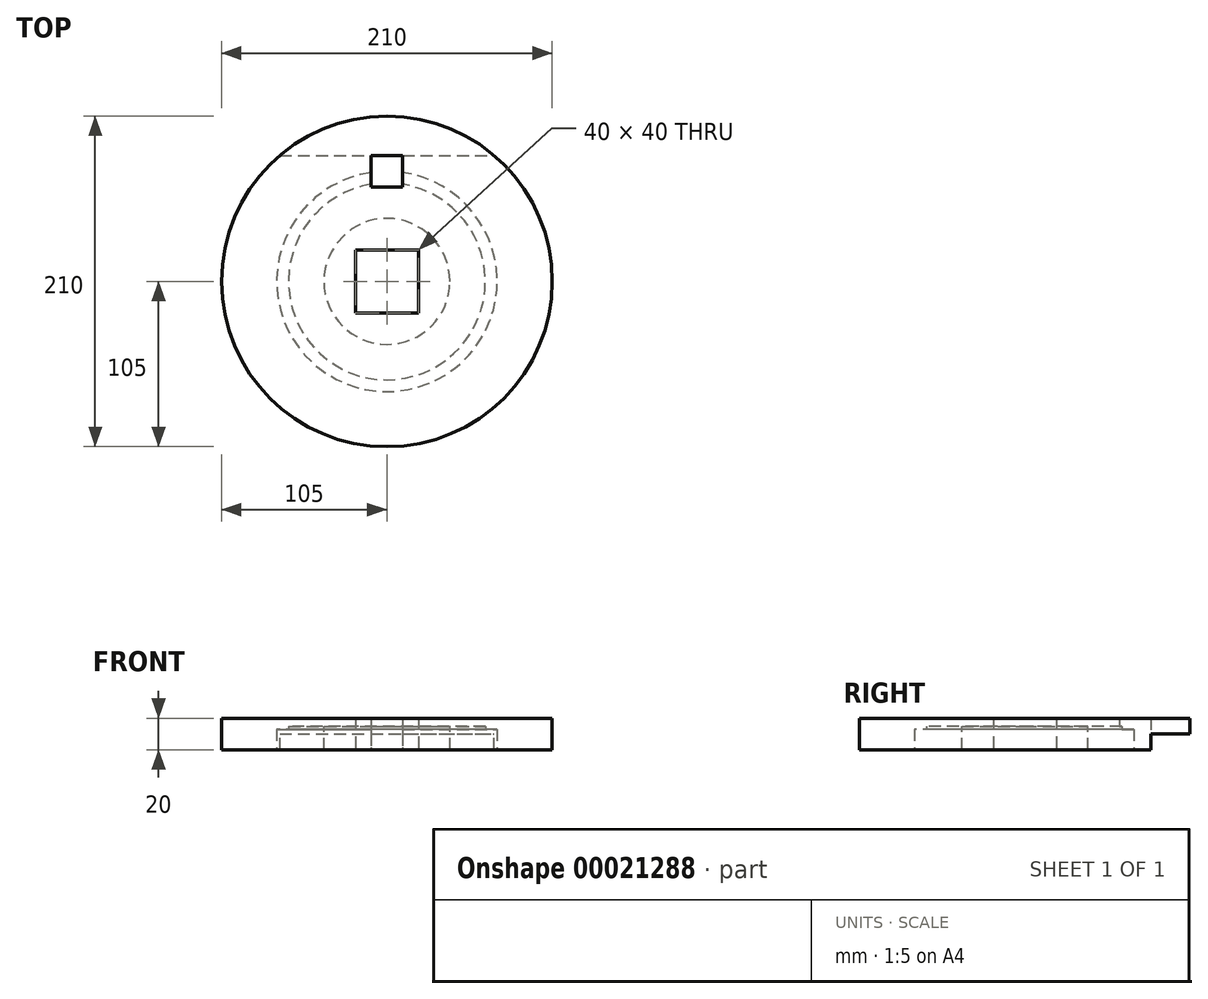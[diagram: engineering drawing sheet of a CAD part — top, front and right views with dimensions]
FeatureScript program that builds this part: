
annotation { "Feature Type Name" : "Feature", "Feature Type Description" : "" }
export const myFeature = defineFeature(function(context is Context, id is Id, definition is map)
    precondition{}
    {
        {
            var Q0;
            Q0=qCreatedBy(makeId("Top.planeOp"),FACE);
            var sketch = newSketch(context, id + "F0", { "sketchPlane" : qUnion([Q0])});
            skCircle(sketch, "E0", {"center": v(0, 0) * mm, "radius": 105 * mm});
            skSolve(sketch);
        }
        {
            var Q0;
            Q0=makeQuery(id+"F0.imprint","IMPRINT",FACE,{"disambiguationData":[TD([[makeQuery(id+"F0.imprint","IMPRINT",EDGE,{"derivedFrom":sQuery(id+"F0.wireOp",EDGE,"E0")}),1.0]])]});
            extrude(context, id + "F1", {"entities" : qUnion([Q0]), "oppositeDirection" : true, "depth" : 20 * mm});
        }
        {
            var Q0;
            Q0=makeQuery(id+"F1.opExtrude","CAP_FACE",FACE,{"disambiguationData":[OSD([sQuery(id+"F0.wireOp",EDGE,"E0")])],"isStart":false});
            var sketch = newSketch(context, id + "F2", { "sketchPlane" : qUnion([Q0])});
            skCircle(sketch, "E1", {"center": v(0, 0) * mm, "radius": 70 * mm});
            skSolve(sketch);
        }
        {
            var Q0;
            Q0 = qSketchRegion(id + "F2", true);
            extrude(context, id + "F3", {"entities" : qUnion([Q0]), "operationType" : NewBodyOperationType.REMOVE, "oppositeDirection" : true, "depth" : 13 * mm});
        }
        {
            var Q0;
            Q0=makeQuery(id+"F3.boolean.opBoolean","COPY",FACE,{"derivedFrom":makeQuery(id+"F3.opExtrude","CAP_FACE",FACE,{"disambiguationData":[OSD([sQuery(id+"F2.wireOp",EDGE,"E1")])],"isStart":false})});
            var sketch = newSketch(context, id + "F4", { "sketchPlane" : qUnion([Q0])});
            skCircle(sketch, "E2", {"center": v(0, 0) * mm, "radius": 62.5 * mm});
            skSolve(sketch);
        }
        {
            var Q0;
            Q0 = qSketchRegion(id + "F4", true);
            extrude(context, id + "F5", {"entities" : qUnion([Q0]), "operationType" : NewBodyOperationType.REMOVE, "oppositeDirection" : true, "depth" : 2 * mm});
        }
        {
            var Q0;
            Q0=makeQuery(id+"F5.boolean.opBoolean","COPY",FACE,{"derivedFrom":makeQuery(id+"F5.opExtrude","CAP_FACE",FACE,{"disambiguationData":[OSD([sQuery(id+"F4.wireOp",EDGE,"E2")])],"isStart":false})});
            var sketch = newSketch(context, id + "F6", { "sketchPlane" : qUnion([Q0])});
            skCircle(sketch, "E3", {"center": v(0, 0) * mm, "radius": 40 * mm});
            skSolve(sketch);
        }
        {
            var Q0;
            Q0 = qSketchRegion(id + "F6", true);
            extrude(context, id + "F7", {"entities" : qUnion([Q0]), "operationType" : NewBodyOperationType.ADD, "depth" : 15 * mm});
        }
        {
            var Q0;
            Q0=makeQuery(id+"F7.opExtrude","CAP_FACE",FACE,{"disambiguationData":[OSD([sQuery(id+"F6.wireOp",EDGE,"E3")])],"isStart":false});
            var sketch = newSketch(context, id + "F8", { "sketchPlane" : qUnion([Q0])});
            skLineSegment(sketch, "E4.rect.bottom", {"start": v(20, -20) * mm, "end": v(-20, -20) * mm});
            skLineSegment(sketch, "E4.rect.top", {"start": v(20, 20) * mm, "end": v(-20, 20) * mm});
            skLineSegment(sketch, "E4.rect.left", {"start": v(20, -20) * mm, "end": v(20, 20) * mm});
            skLineSegment(sketch, "E4.rect.right", {"start": v(-20, -20) * mm, "end": v(-20, 20) * mm});
            skPoint(sketch, "E4.rect.middle", {"position": v(0, 0) * mm});
            skSolve(sketch);
        }
        {
            var Q0;
            Q0 = qSketchRegion(id + "F8", true);
            var Q1;
            Q1=makeQuery(id+"F1.opExtrude","CAP_FACE",FACE,{"disambiguationData":[OSD([sQuery(id+"F0.wireOp",EDGE,"E0")])],"isStart":true});
            extrude(context, id + "F9", {"entities" : qUnion([Q0]), "operationType" : NewBodyOperationType.REMOVE, "endBound" : BoundingType.UP_TO_SURFACE, "oppositeDirection" : true, "endBoundEntityFace" : qUnion([Q1]), "depth" : 25 * mm});
        }
        {
            var Q0;
            Q0=makeQuery(id+"F1.opExtrude","CAP_FACE",FACE,{"disambiguationData":[OSD([sQuery(id+"F0.wireOp",EDGE,"E0")])],"isStart":false});
            var sketch = newSketch(context, id + "F10", { "sketchPlane" : qUnion([Q0])});
            skLineSegment(sketch, "E5.bottom", {"start": v(-10, -60) * mm, "end": v(10, -60) * mm});
            skLineSegment(sketch, "E5.top", {"start": v(-10, -80) * mm, "end": v(10, -80) * mm});
            skLineSegment(sketch, "E5.left", {"start": v(-10, -60) * mm, "end": v(-10, -80) * mm});
            skLineSegment(sketch, "E5.right", {"start": v(10, -60) * mm, "end": v(10, -80) * mm});
            skSolve(sketch);
        }
        {
            var Q0;
            Q0 = qSketchRegion(id + "F10", true);
            var Q1;
            Q1=makeQuery(id+"F1.opExtrude","CAP_FACE",FACE,{"disambiguationData":[OSD([sQuery(id+"F0.wireOp",EDGE,"E0")])],"isStart":true});
            extrude(context, id + "F11", {"entities" : qUnion([Q0]), "operationType" : NewBodyOperationType.REMOVE, "endBound" : BoundingType.UP_TO_SURFACE, "oppositeDirection" : true, "endBoundEntityFace" : qUnion([Q1]), "depth" : 25 * mm});
        }
        {
            var Q0;
            Q0=makeQuery(id+"F1.opExtrude","CAP_FACE",FACE,{"disambiguationData":[OSD([sQuery(id+"F0.wireOp",EDGE,"E0")])],"isStart":false});
            var sketch = newSketch(context, id + "F12", { "sketchPlane" : qUnion([Q0])});
            skLineSegment(sketch, "E6.bottom", {"start": v(-70, -80) * mm, "end": v(70, -80) * mm});
            skLineSegment(sketch, "E6.top", {"start": v(-70, -110) * mm, "end": v(70, -110) * mm});
            skLineSegment(sketch, "E6.left", {"start": v(-70, -80) * mm, "end": v(-70, -110) * mm});
            skLineSegment(sketch, "E6.right", {"start": v(70, -80) * mm, "end": v(70, -110) * mm});
            skSolve(sketch);
        }
        {
            var Q0;
            Q0 = qSketchRegion(id + "F12", true);
            extrude(context, id + "F13", {"entities" : qUnion([Q0]), "operationType" : NewBodyOperationType.REMOVE, "oppositeDirection" : true, "depth" : 10 * mm});
        }
    });
